# Revit family: Скамейка стальная «Леман» Арт 14901
name_source: partatom
category: Антураж
revit_build: Autodesk Revit 2018 (Build: 20180423_1000(x64)
units: mm (PartAtom-declared; Revit-internal decimal feet)

## family parameters
Всегда вертикально = Да
Источник визуального образа = Геометрия семейства
На основе рабочей плоскости = Нет
Общий = Нет
При загрузке вырезать с полостями = Нет
Точка расчета площади = Нет

## types (8) — shared parameters
URL = https://hobbyka.ru
Артикул товара = Арт. 14901
Высота = 794 мм
Группа модели = Скамейки
Изготовитель = ООО «Хоббика»
Ширина = 615 мм

## per-type parameters (varying)
| type | Версия 1,5 м АС | Версия 1,5 м К | Версия 1,5 м Л | Версия 1,5 м Н+К | Версия 1,8 м АС | Версия 1,8 м К | Версия 2,0 м АС (2 опоры) | Версия 2,0 м К (2 опоры) | Длина | Изображение типоразмера | Материал изделия | Описание | Цвет опоры | Цвет сидения |
| Версия 1,5 м Ангарская сосна | Да | Нет | Нет | Нет | Нет | Нет | Нет | Нет | 1500 мм | Скамейка стальная «Леман» Арт 14901 АС.jpg | Сталь, дерево | Скамейка стальная «Леман». Версия 1,5 м Ангарская сосна | Сталь | Ангарская сосна |
| Версия 1,5 м Лиственница | Нет | Нет | Да | Нет | Нет | Нет | Нет | Нет | 1500 мм | Скамейка стальная «Леман» Арт 14901 АС.jpg | Сталь, дерево | Скамейка стальная «Леман». Версия 1,5 м Лиственница | Сталь | Лиственница |
| Версия 1,5 м Композит | Нет | Да | Нет | Нет | Нет | Нет | Нет | Нет | 1500 мм | Скамейка стальная «Леман» Арт 14901 К.jpg | Сталь, композит | Скамейка стальная «Леман». Версия 1,5 м Композит | Сталь | Композит |
| Версия 1,5 м Нержавеющая сталь плюс композит | Нет | Нет | Нет | Да | Нет | Нет | Нет | Нет | 1500 мм | Скамейка стальная «Леман» Арт 14901 К.jpg | Нержавеющая сталь, композит | Скамейка стальная «Леман». Версия 1,5 м Нержавеющая сталь плюс композит | Нержавеющая сталь | Композит |
| Версия 1,8 м Ангарская сосна | Нет | Нет | Нет | Нет | Да | Нет | Нет | Нет | 1800 мм | Скамейка стальная «Леман» Арт 14901 АС.jpg | Сталь, дерево | Скамейка стальная «Леман». Версия 1,8 м Ангарская сосна | Сталь | Ангарская сосна |
| Версия 1,8 м Композит | Нет | Нет | Нет | Нет | Нет | Да | Нет | Нет | 1800 мм | Скамейка стальная «Леман» Арт 14901 К.jpg | Сталь, композит | Скамейка стальная «Леман». Версия 1,8 м Композит | Сталь | Композит |
| Версия 2,0 м Ангарская сосна (2 опоры) | Нет | Нет | Нет | Нет | Нет | Нет | Да | Нет | 2000 мм | Скамейка стальная «Леман» Арт 14901 АС.jpg | Сталь, дерево | Скамейка стальная «Леман». Версия 2,0 м Ангарская сосна (2 опоры) | Сталь | Ангарская сосна |
| Версия 2,0 м Композит (2 опоры) | Нет | Нет | Нет | Нет | Нет | Нет | Нет | Да | 2000 мм | Скамейка стальная «Леман» Арт 14901 К.jpg | Сталь, композит | Скамейка стальная «Леман». Версия 2,0 м Композит (2 опоры) | Сталь | Композит |
